# Revit family: UNB_Eurovit+_R0268_BIM_NL
name_source: partatom
category: Plumbing Fixtures
units: mm (PartAtom-declared; Revit-internal decimal feet)

## family parameters
Cut with Voids When Loaded = No
Host = Face
Maintain Annotation Orientation = No
OmniClass Number = 23.45.05.14.21.11
OmniClass Title = Bath/Shower Units
Part Type = Normal
Room Calculation Point = No
Round Connector Dimension = Use Diameter
Shared = Yes

## types (4) — shared parameters
Accesoires = https://www.idealstandard.nl
Accessories = https://www.idealstandard.nl
Afmetingen = 1500 x 300 x 236 mm
AfstandsEenheid = millimeter
AreaUnits = millimeter
Assembly Code = C1030200
AssetType = Vast
Auteur = Ideal Standard
BIMObjectName = ISI_IdealStandard_Furniture_R0268
BREEAM = No
BimObjectNaam = ISI_IdealStandard_Furniture_R0268
Brand = Unbranded
Breedte = 300
ConnectionType = sanitair
CurrencyUnit = €
Default Elevation = 1219 mm
Diepte = 235,99999999997
DurationUnit = jaar
DuurEenheid = jaar
ECA = No
EPD = https://www.idealstandard.nl
ExpectedLife = 30
GemaaktOp = 26/06/2024
Help = https://www.idealstandard.nl
Hoogte = 1500
Hulp = https://www.idealstandard.nl
IfcExportAs = IfcFurnitureType
Installatieinstructies = https://www.idealstandard.nl
InstallationInstructions = https://www.idealstandard.nl
Lengte = 235,99999999997
LinearUnits = millimeters
Manufacturer = Ideal Standard
ManufacturerURL = https://www.idealstandard.nl
Materiaal = Furniture
Merk = Merkloos
NBSDescription = Baths
Name = ISI_Furniture_Unb_R0268_IdealStandard
NettWeight = Kg
Nettogewicht = Kg
NominalDepth = 236 mm
NominalHeight = 1500 mm  [stored 4.92126 ft]
NominalLength = 236 mm
NominalWidth = 300 mm
ProductInformation = https://www.idealstandard.nl
ProductSoort = meubels
Productinformatie = https://www.idealstandard.nl
Shape = Rechthoekig
Size = 1500 x 300 x 236 mm
Space = Intern
SpareParts = https://www.idealstandard.nl
TMV3 = No
Telefoonnummer = 077 355 08 08
Typeconnectie = sanitair
URL = https://www.idealstandard.nl
Uniclass2015Code = Pr_40_20_76
Uniclass2015Title = Sanitary accessories
Uniclass2015Version = Products v1.34
Urlproducent = https://www.idealstandard.nl
ValutaEenheid = €
Versie = 1
Version = 1
VolumeUnits = Liter
Volumeunits = Liter
Vorm = Rechthoekig
WRAS = No
WaarborgGarantieInstallatie = Fabrieksgarantie
WarrantyDescription = Manufacturers Warranty
WarrantyDurationParts = 2
WarrantyDurationUnit = year
WarrantyGuarantorParts = https://www.idealstandard.nl
WaterEfficientProduct = No
Wisselstukken = https://www.idealstandard.nl
zero-valued in all types: Vervangingskosten

## per-type parameters (varying)
| type | Afwerking | Artikelnummer | Artikelomschrijving | BarCode | Color | Description | Eigenschappen | Features | Finish | Kleur | MAT | Model | ModelNumber | ModelReference |
| R0268WG - TALL UNIT 30x27 2 DOORS GLOSSY WHITE | Glanzend wit | R0268WG | Eurovit 2.0 HOGE KAST 30x27 2 DEUREN GLANZEND WIT | 3391500589193 | Glanzend wit | Eurovit 2.0 HOGE KAST 30x27 2 DEUREN GLANZEND WIT | Eurovit 2.0 HOGE KAST 30x27 2 DEUREN GLANZEND WIT | Eurovit 2.0 HOGE KAST 30x27 2 DEUREN GLANZEND WIT | Glanzend wit | Glanzend wit | WG-White | R0268WG | R0268WG | Eurovit 2.0 HOGE KAST 30x27 2 DEUREN GLANZEND WIT |
| R0268Y8 - TALL UNIT 30x27 2 DOORS NATURAL OAK | Natuurlijk eiken | R0268Y8 | Eurovit 2.0 HOGE KAST 30x27 2 DEUREN NATUURLIJK EIKEN | 3391500589209 | Natuurlijk eiken | Eurovit 2.0 HOGE KAST 30x27 2 DEUREN NATUURLIJK EIKEN | Eurovit 2.0 HOGE KAST 30x27 2 DEUREN NATUURLIJK EIKEN | Eurovit 2.0 HOGE KAST 30x27 2 DEUREN NATUURLIJK EIKEN | Natuurlijk eiken | Natuurlijk eiken | Y8 | R0268Y8 | R0268Y8 | Eurovit 2.0 HOGE KAST 30x27 2 DEUREN NATUURLIJK EIKEN |
| R0268Y9 - TALL UNIT 30x27 2 DOORS FLINT HICKORY | Flint-Hickory | R0268Y9 | Eurovit 2.0 HOGE KAST 30x27 2 DEUREN FLINT HICKORY | 3391500589216 | Flint-Hickory | Eurovit 2.0 HOGE KAST 30x27 2 DEUREN FLINT HICKORY | Eurovit 2.0 HOGE KAST 30x27 2 DEUREN FLINT HICKORY | Eurovit 2.0 HOGE KAST 30x27 2 DEUREN FLINT HICKORY | Flint-Hickory | Flint-Hickory | Y9 | R0268Y9 | R0268Y9 | Eurovit 2.0 HOGE KAST 30x27 2 DEUREN FLINT HICKORY |
| R0268TI - TALL UNIT 30x27 2 DOORS MID GREY | Middengrijs | R0268TI | Eurovit 2.0 HOGE KAST 30x27 2 DEUREN MIDDENGRIJS | 3391500589186 | Middengrijs | Eurovit 2.0 HOGE KAST 30x27 2 DEUREN MIDDENGRIJS | Eurovit 2.0 HOGE KAST 30x27 2 DEUREN MIDDENGRIJS | Eurovit 2.0 HOGE KAST 30x27 2 DEUREN MIDDENGRIJS | Middengrijs | Middengrijs | TI | R0268TI | R0268TI | Eurovit 2.0 HOGE KAST 30x27 2 DEUREN MIDDENGRIJS |

note: [stored X ft] marks values corroborated as IEEE doubles in the binary element streams (Revit-internal decimal feet)

## geometry (parser evidence)
native form markers: Sweep x2
no freeform markers — native parametric forms only
